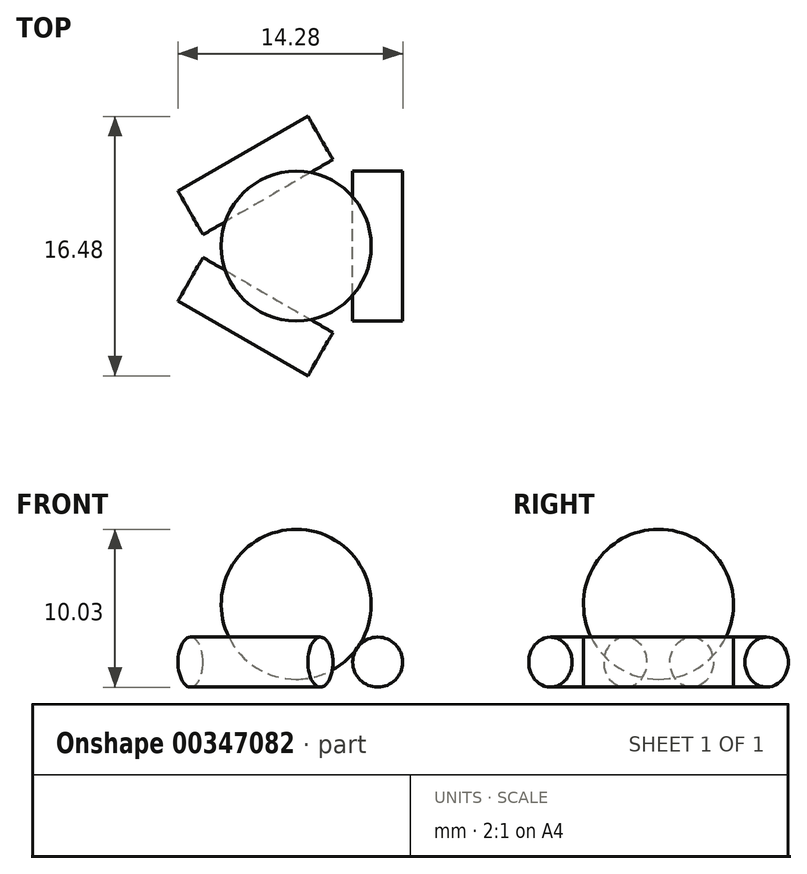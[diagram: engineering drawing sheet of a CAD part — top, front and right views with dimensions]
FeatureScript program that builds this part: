
annotation { "Feature Type Name" : "Feature", "Feature Type Description" : "" }
export const myFeature = defineFeature(function(context is Context, id is Id, definition is map)
    precondition{}
    {
        {
            var Q0;
            Q0=qCreatedBy(makeId("Top.planeOp"),FACE);
            var sketch = newSketch(context, id + "F0", { "sketchPlane" : qUnion([Q0])});
            skCircle(sketch, "E0.cCircle", {"center": v(0, 0) * mm, "radius": 5.18 * mm, "construction": true});
            skLineSegment(sketch, "E0.0", {"start": v(5.18, 8.97) * mm, "end": v(5.18, -8.97) * mm, "construction": true});
            skLineSegment(sketch, "E0.1", {"start": v(5.18, -8.97) * mm, "end": v(-10.36, 0) * mm, "construction": true});
            skLineSegment(sketch, "E0.2", {"start": v(-10.36, 0) * mm, "end": v(5.18, 8.97) * mm});
            skPoint(sketch, "E0.0.midPoint", {"position": v(5.18, 0) * mm});
            skLineSegment(sketch, "E1", {"start": v(-5.92, 0.73) * mm, "end": v(-6.71, 2.1) * mm});
            skLineSegment(sketch, "E2", {"start": v(-7.5, 3.48) * mm, "end": v(0.74, 8.24) * mm, "construction": true});
            skPoint(sketch, "E3", {"position": v(-6.71, 2.1) * mm});
            skLineSegment(sketch, "E4", {"start": v(-5.92, 0.73) * mm, "end": v(2.33, 5.5) * mm});
            skLineSegment(sketch, "E5", {"start": v(2.33, 5.5) * mm, "end": v(1.54, 6.87) * mm});
            skPoint(sketch, "E6", {"position": v(-1.8, 3.1) * mm});
            skLineSegment(sketch, "E7", {"start": v(0, 0) * mm, "end": v(-2.59, 4.48) * mm, "construction": true});
            skCircle(sketch, "E8", {"center": v(0, 0) * mm, "radius": 3.6 * mm});
            skPoint(sketch, "E8.first.point", {"position": v(1.8, -3.1) * mm});
            skPoint(sketch, "E8.third.point", {"position": v(1.8, -3.1) * mm});
            skLineSegment(sketch, "E9", {"start": v(-6.71, 2.1) * mm, "end": v(-7.5, 3.48) * mm, "construction": true});
            skLineSegment(sketch, "E10", {"start": v(1.54, 6.87) * mm, "end": v(0.74, 8.24) * mm, "construction": true});
            skLineSegment(sketch, "E11.1.0", {"start": v(2.33, -5.5) * mm, "end": v(1.54, -6.87) * mm});
            skLineSegment(sketch, "E11.1.1", {"start": v(5.18, -8.97) * mm, "end": v(-10.36, 0) * mm});
            skLineSegment(sketch, "E11.1.2", {"start": v(2.33, -5.5) * mm, "end": v(-5.92, -0.73) * mm});
            skLineSegment(sketch, "E11.1.3", {"start": v(-5.92, -0.73) * mm, "end": v(-6.71, -2.1) * mm});
            skLineSegment(sketch, "E11.2.0", {"start": v(3.6, 4.76) * mm, "end": v(5.18, 4.76) * mm});
            skLineSegment(sketch, "E11.2.1", {"start": v(5.18, 8.97) * mm, "end": v(5.18, -8.97) * mm});
            skLineSegment(sketch, "E11.2.2", {"start": v(3.6, 4.76) * mm, "end": v(3.6, -4.76) * mm});
            skLineSegment(sketch, "E11.2.3", {"start": v(3.6, -4.76) * mm, "end": v(5.18, -4.76) * mm});
            skSolve(sketch);
        }
        {
            var Q0;
            {var subQ3=sQuery(id+"F0.wireOp",EDGE,"E1");Q0=makeQuery(id+"F0.imprint","IMPRINT",FACE,{"disambiguationData":[TD([[makeQuery(id+"F0.imprint","IMPRINT",EDGE,{"derivedFrom":subQ3}),-1.0]])]});}
            var Q1;
            Q1=sQuery(id+"F0.wireOp",EDGE,"E0.2");
            revolve(context, id + "F1", {"entities" : qUnion([Q0]), "axis" : qUnion([Q1]), "revolveType" : RevolveType.FULL});
        }
        {
            var Q0;
            Q0=qCreatedBy(makeId("Front.planeOp"),FACE);
            var sketch = newSketch(context, id + "F2", { "sketchPlane" : qUnion([Q0])});
            skLineSegment(sketch, "E12", {"start": v(0, 0) * mm, "end": v(0, 12.2) * mm, "construction": true});
            skPoint(sketch, "E13.0", {"position": v(1.8, 0) * mm});
            skSolve(sketch);
        }
        {
            var Q0;
            Q0=makeQuery(id+"F1.opRevolve","SWEPT_BODY",BODY,{"disambiguationData":[OSD([sQuery(id+"F0.wireOp",EDGE,"E0.2"),sQuery(id+"F0.wireOp",EDGE,"E1"),sQuery(id+"F0.wireOp",EDGE,"E4"),sQuery(id+"F0.wireOp",EDGE,"E5")])]});
            var Q1;
            Q1=sQuery(id+"F2.wireOp",EDGE,"E12");
            circularPattern(context, id + "F3", {"entities" : qUnion([Q0]), "axis" : qUnion([Q1]), "angle" : 360 * degree, "instanceCount" : 3, "equalSpace" : true, "computeTransformsWithoutBuiltin" : true});
        }
        {
            var Q0;
            Q0=qCreatedBy(makeId("Front.planeOp"),FACE);
            var sketch = newSketch(context, id + "F4", { "sketchPlane" : qUnion([Q0])});
            skLineSegment(sketch, "E14.0", {"start": v(0, 0) * mm, "end": v(0, 12.2) * mm, "construction": true});
            skCircle(sketch, "E15", {"center": v(5.18, 0) * mm, "radius": 1.59 * mm});
            skPoint(sketch, "E16", {"position": v(0, 8.44) * mm});
            skLineSegment(sketch, "E17", {"start": v(0, 0) * mm, "end": v(0, -3.33) * mm, "construction": true});
            skPoint(sketch, "E18", {"position": v(0, -1.09) * mm});
            skArc(sketch, "E19", {"start": v(0, 8.44) * mm, "mid": v(-4.76, 3.68) * mm, "end": v(0, -1.09) * mm, "construction": true});
            skArc(sketch, "E20", {"start": v(0, -1.09) * mm, "mid": v(4.76, 3.68) * mm, "end": v(0, 8.44) * mm});
            skLineSegment(sketch, "E21", {"start": v(0, 8.44) * mm, "end": v(0, -1.09) * mm});
            skSolve(sketch);
        }
        {
            var Q0;
            {var subQ0=sQuery(id+"F4.wireOp",EDGE,"E21");Q0=makeQuery(id+"F4.imprint","IMPRINT",FACE,{"disambiguationData":[TD([[makeQuery(id+"F4.imprint","IMPRINT",EDGE,{"derivedFrom":subQ0}),1.0]])]});}
            var Q1;
            Q1=sQuery(id+"F4.wireOp",EDGE,"E14.0");
            revolve(context, id + "F5", {"entities" : qUnion([Q0]), "axis" : qUnion([Q1]), "revolveType" : RevolveType.FULL});
        }
    });
